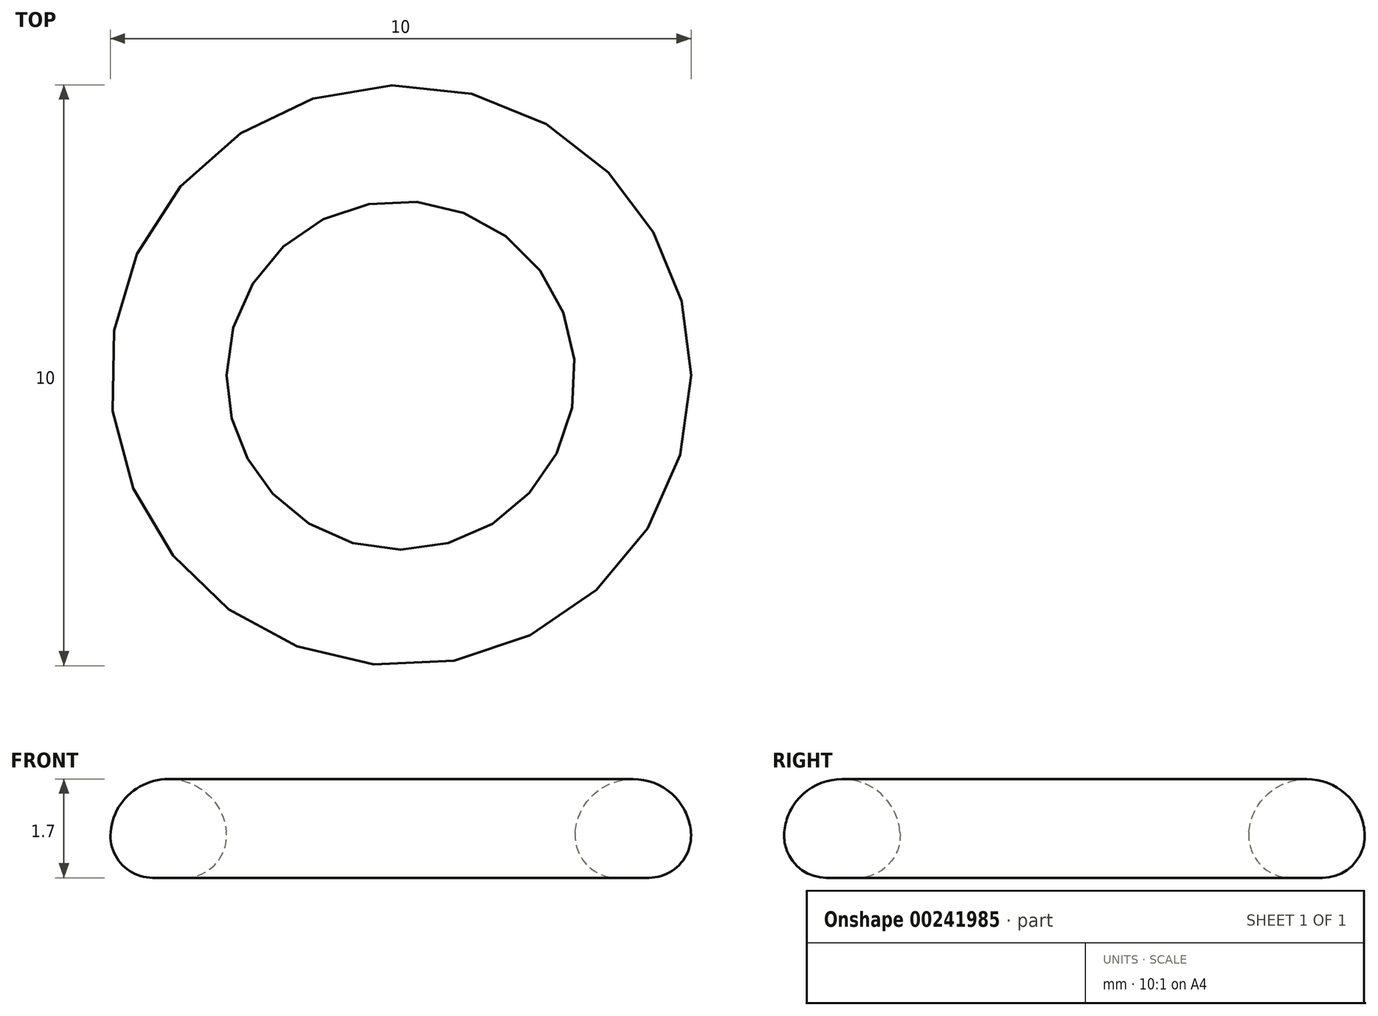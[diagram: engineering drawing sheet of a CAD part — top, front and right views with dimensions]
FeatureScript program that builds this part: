
annotation { "Feature Type Name" : "Feature", "Feature Type Description" : "" }
export const myFeature = defineFeature(function(context is Context, id is Id, definition is map)
    precondition{}
    {
        {
            var Q0;
            Q0=qCreatedBy(makeId("Top.planeOp"),FACE);
            var sketch = newSketch(context, id + "F0", { "sketchPlane" : qUnion([Q0])});
            skCircle(sketch, "E0", {"center": v(0, 0) * mm, "radius": 3 * mm});
            skCircle(sketch, "E1", {"center": v(0, 0) * mm, "radius": 5 * mm});
            skSolve(sketch);
        }
        {
            var Q0;
            Q0=makeQuery(id+"F0.imprint","IMPRINT",FACE,{"disambiguationData":[TD([[makeQuery(id+"F0.imprint","IMPRINT",EDGE,{"derivedFrom":sQuery(id+"F0.wireOp",EDGE,"E0")}),-1.0]])]});
            extrude(context, id + "F1", {"entities" : qUnion([Q0]), "depth" : 1.7 * mm});
        }
        {
            var Q0;
            Q0=makeQuery(id+"F1.opExtrude","CAP_EDGE",EDGE,{"disambiguationData":[OSD([sQuery(id+"F0.wireOp",EDGE,"E1")])],"isStart":false});
            var Q1;
            Q1=makeQuery(id+"F1.opExtrude","CAP_EDGE",EDGE,{"disambiguationData":[OSD([sQuery(id+"F0.wireOp",EDGE,"E0")])],"isStart":false});
            fillet(context, id + "F2", {"entities" : qUnion([Q0, Q1]), "radius" : 1 * mm, "tangentPropagation" : true, "allowEdgeOverflow" : false});
        }
        {
            var Q0;
            Q0=makeQuery(id+"F1.opExtrude","CAP_EDGE",EDGE,{"disambiguationData":[OSD([sQuery(id+"F0.wireOp",EDGE,"E1")])],"isStart":true});
            var Q1;
            Q1=makeQuery(id+"F1.opExtrude","CAP_EDGE",EDGE,{"disambiguationData":[OSD([sQuery(id+"F0.wireOp",EDGE,"E0")])],"isStart":true});
            fillet(context, id + "F3", {"entities" : qUnion([Q0, Q1]), "radius" : 0.72 * mm, "tangentPropagation" : true, "allowEdgeOverflow" : false});
        }
    });
